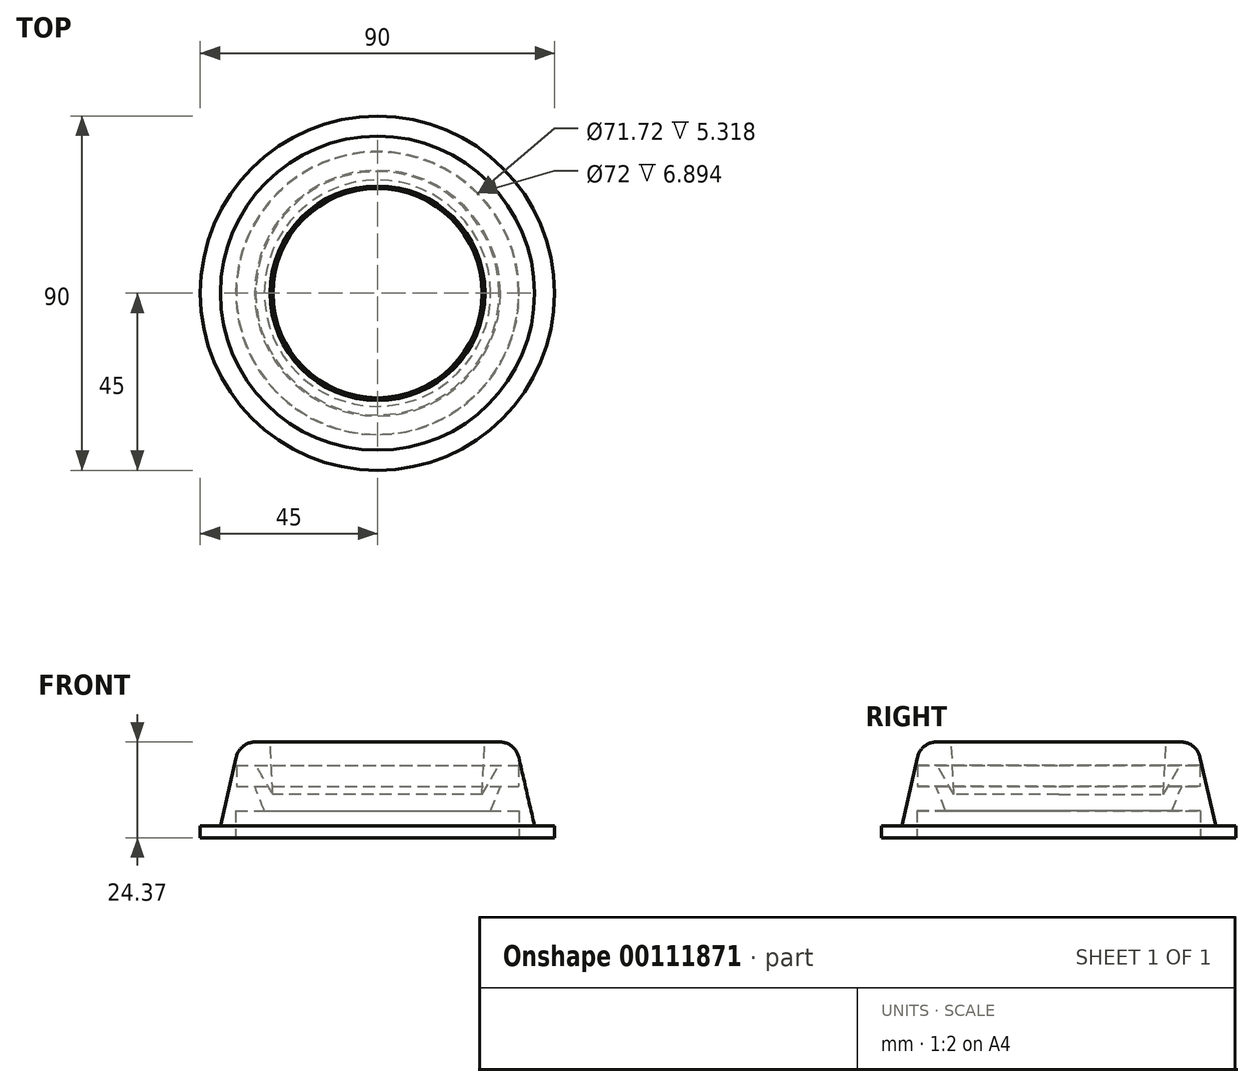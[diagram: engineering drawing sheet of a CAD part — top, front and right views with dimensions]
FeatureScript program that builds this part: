
annotation { "Feature Type Name" : "Feature", "Feature Type Description" : "" }
export const myFeature = defineFeature(function(context is Context, id is Id, definition is map)
    precondition{}
    {
        {
            var Q0;
            Q0=qCreatedBy(makeId("Top.planeOp"),FACE);
            var sketch = newSketch(context, id + "F0", { "sketchPlane" : qUnion([Q0])});
            skCircle(sketch, "E0", {"center": v(0, 0) * mm, "radius": 45 * mm});
            skSolve(sketch);
        }
        {
            var Q0;
            Q0 = qSketchRegion(id + "F0", true);
            extrude(context, id + "F1", {"entities" : qUnion([Q0]), "flatOperationType" : FlatOperationType.REMOVE, "offsetDistance" : 25.4 * mm, "depth" : 3 * mm, "domain" : OperationDomain.MODEL});
        }
        {
            var Q0;
            Q0=qCreatedBy(makeId("Front.planeOp"),FACE);
            var sketch = newSketch(context, id + "F2", { "sketchPlane" : qUnion([Q0])});
            skLineSegment(sketch, "E1", {"start": v(0, 0) * mm, "end": v(0, 24.37) * mm});
            skLineSegment(sketch, "E2", {"start": v(-40.59, 0) * mm, "end": v(0, 0) * mm});
            skLineSegment(sketch, "E3", {"start": v(0, 27.26) * mm, "end": v(0, -65.9) * mm, "construction": true});
            skLineSegment(sketch, "E4", {"start": v(0, 24.37) * mm, "end": v(-35, 24.37) * mm});
            skLineSegment(sketch, "E5", {"start": v(-35, 24.37) * mm, "end": v(-40.59, 0) * mm});
            skSolve(sketch);
        }
        {
            var Q0;
            Q0=makeQuery(id+"F2.imprint","IMPRINT",FACE,{"disambiguationData":[TD([[makeQuery(id+"F2.imprint","IMPRINT",EDGE,{"derivedFrom":sQuery(id+"F2.wireOp",EDGE,"E1")}),1.0]])]});
            var Q1;
            Q1=sQuery(id+"F2.wireOp",EDGE,"E3");
            revolve(context, id + "F3", {"operationType" : NewBodyOperationType.ADD, "surfaceOperationType" : NewSurfaceOperationType.NEW, "entities" : qUnion([Q0]), "axis" : qUnion([Q1]), "revolveType" : RevolveType.FULL, "oppositeDirection" : true});
        }
        {
            var Q0;
            Q0=makeQuery(id+"F3.opRevolve","SWEPT_EDGE",EDGE,{"disambiguationData":[OSD([sQuery(id+"F2.wireOp",EDGE,"E4"),sQuery(id+"F2.wireOp",EDGE,"E5")])]});
            fillet(context, id + "F4", {"entities" : qUnion([Q0]), "radius" : 5.08 * mm, "tangentPropagation" : true, "defaultsChanged" : false, "vertexSettings" : [], "allowEdgeOverflow" : false});
        }
        {
            var Q0;
            Q0=qCreatedBy(makeId("Top.planeOp"),FACE);
            var sketch = newSketch(context, id + "F5", { "sketchPlane" : qUnion([Q0])});
            skCircle(sketch, "E6", {"center": v(0, 0) * mm, "radius": 26 * mm});
            skSolve(sketch);
        }
        {
            var Q0;
            Q0 = qSketchRegion(id + "F5", true);
            extrude(context, id + "F6", {"entities" : qUnion([Q0]), "operationType" : NewBodyOperationType.REMOVE, "flatOperationType" : FlatOperationType.REMOVE, "endBound" : BoundingType.SYMMETRIC, "oppositeDirection" : true, "offsetDistance" : 25.4 * mm, "depth" : 75.75 * mm, "hasDraft" : true, "draftAngle" : 3 * degree, "domain" : OperationDomain.MODEL});
        }
        {
            var Q0;
            Q0=qCreatedBy(makeId("Front.planeOp"),FACE);
            var sketch = newSketch(context, id + "F7", { "sketchPlane" : qUnion([Q0])});
            skLineSegment(sketch, "E7", {"start": v(30.92, 18.43) * mm, "end": v(35.86, 18.43) * mm});
            skLineSegment(sketch, "E8", {"start": v(35.86, 18.43) * mm, "end": v(35.86, 13.11) * mm});
            skLineSegment(sketch, "E9", {"start": v(35.86, 13.11) * mm, "end": v(31.22, 13.11) * mm});
            skLineSegment(sketch, "E10", {"start": v(31.22, 13.11) * mm, "end": v(26.02, 0) * mm});
            skLineSegment(sketch, "E11", {"start": v(0, 66.7) * mm, "end": v(0, -38.37) * mm, "construction": true});
            skLineSegment(sketch, "E12", {"start": v(30.92, 18.43) * mm, "end": v(20.12, 0) * mm});
            skLineSegment(sketch, "E13", {"start": v(20.12, 0) * mm, "end": v(26.02, 0) * mm});
            skSolve(sketch);
        }
        {
            var Q0;
            Q0=makeQuery(id+"F7.imprint","IMPRINT",FACE,{"disambiguationData":[TD([[makeQuery(id+"F7.imprint","IMPRINT",EDGE,{"derivedFrom":sQuery(id+"F7.wireOp",EDGE,"E7")}),-1.0]])]});
            var Q1;
            Q1=sQuery(id+"F7.wireOp",EDGE,"E11");
            revolve(context, id + "F8", {"operationType" : NewBodyOperationType.REMOVE, "surfaceOperationType" : NewSurfaceOperationType.NEW, "entities" : qUnion([Q0]), "axis" : qUnion([Q1]), "revolveType" : RevolveType.FULL, "oppositeDirection" : true});
        }
        {
            var Q0;
            Q0=makeQuery(id+"F1.opExtrude","CAP_FACE",FACE,{"disambiguationData":[OSD([sQuery(id+"F0.wireOp",EDGE,"E0")])],"isStart":true});
            var sketch = newSketch(context, id + "F9", { "sketchPlane" : qUnion([Q0])});
            skCircle(sketch, "E14", {"center": v(0, 0) * mm, "radius": 36 * mm});
            skSolve(sketch);
        }
        {
            var Q0;
            Q0 = qSketchRegion(id + "F9", true);
            extrude(context, id + "F10", {"entities" : qUnion([Q0]), "operationType" : NewBodyOperationType.REMOVE, "flatOperationType" : FlatOperationType.REMOVE, "oppositeDirection" : true, "offsetDistance" : 25.4 * mm, "depth" : 6.9 * mm, "domain" : OperationDomain.MODEL});
        }
    });
